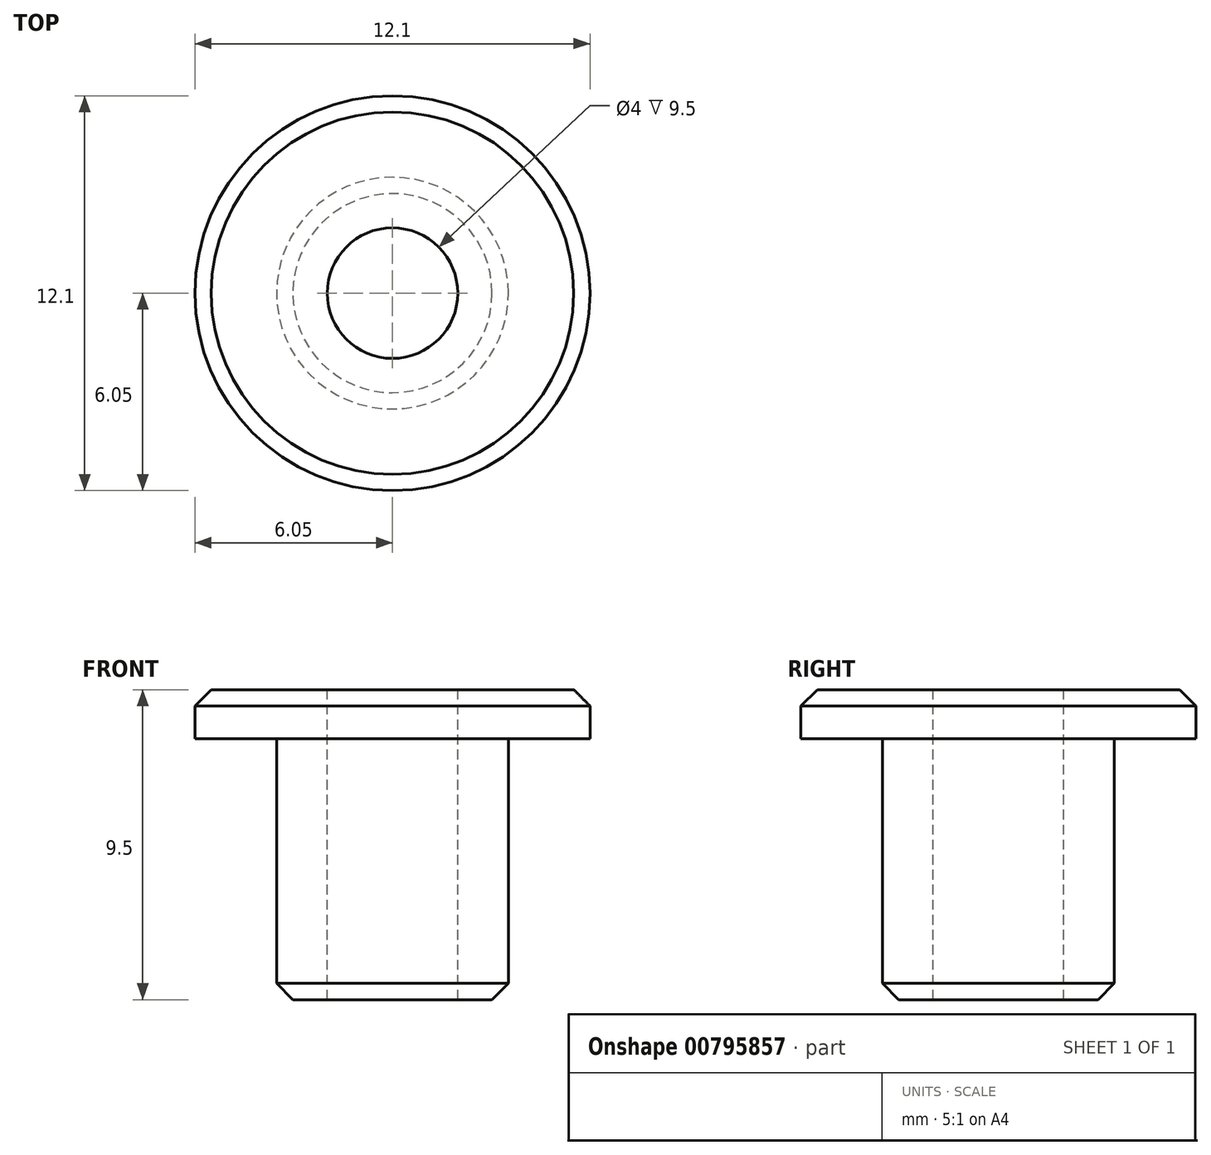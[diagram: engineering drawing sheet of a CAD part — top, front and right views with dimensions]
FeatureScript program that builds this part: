
annotation { "Feature Type Name" : "Feature", "Feature Type Description" : "" }
export const myFeature = defineFeature(function(context is Context, id is Id, definition is map)
    precondition{}
    {
        {
            var Q0;
            Q0=qCreatedBy(makeId("Front.planeOp"),FACE);
            var sketch = newSketch(context, id + "F0", { "sketchPlane" : qUnion([Q0])});
            skLineSegment(sketch, "E0", {"start": v(0, -4.75) * mm, "end": v(3.05, -4.75) * mm});
            skLineSegment(sketch, "E1", {"start": v(3.05, -4.75) * mm, "end": v(3.55, -4.25) * mm});
            skLineSegment(sketch, "E2", {"start": v(3.55, -4.25) * mm, "end": v(3.55, 3.25) * mm});
            skLineSegment(sketch, "E3", {"start": v(3.55, 3.25) * mm, "end": v(6.05, 3.25) * mm});
            skLineSegment(sketch, "E4", {"start": v(6.05, 3.25) * mm, "end": v(6.05, 4.25) * mm});
            skLineSegment(sketch, "E5", {"start": v(6.05, 4.25) * mm, "end": v(5.55, 4.75) * mm});
            skLineSegment(sketch, "E6", {"start": v(5.55, 4.75) * mm, "end": v(0, 4.75) * mm});
            skLineSegment(sketch, "E7", {"start": v(0, 4.75) * mm, "end": v(0, -4.75) * mm});
            skSolve(sketch);
        }
        {
            var Q0;
            Q0 = qSketchRegion(id + "F0", true);
            var Q1;
            Q1=sQuery(id+"F0.wireOp",EDGE,"E7");
            revolve(context, id + "F1", {"surfaceOperationType" : NewSurfaceOperationType.NEW, "entities" : qUnion([Q0]), "axis" : qUnion([Q1]), "revolveType" : RevolveType.FULL});
        }
        {
            var Q0;
            Q0=makeQuery(id+"F1.opRevolve","SWEPT_FACE",FACE,{"disambiguationData":[OSD([sQuery(id+"F0.wireOp",EDGE,"E6")])]});
            var sketch = newSketch(context, id + "F2", { "sketchPlane" : qUnion([Q0])});
            skCircle(sketch, "E8", {"center": v(0, 0) * mm, "radius": 2 * mm});
            skSolve(sketch);
        }
        {
            var Q0;
            Q0 = qSketchRegion(id + "F2", true);
            extrude(context, id + "F3", {"entities" : qUnion([Q0]), "operationType" : NewBodyOperationType.REMOVE, "endBound" : BoundingType.THROUGH_ALL, "oppositeDirection" : true, "depth" : 25 * mm, "offsetDistance" : 25 * mm});
        }
    });
